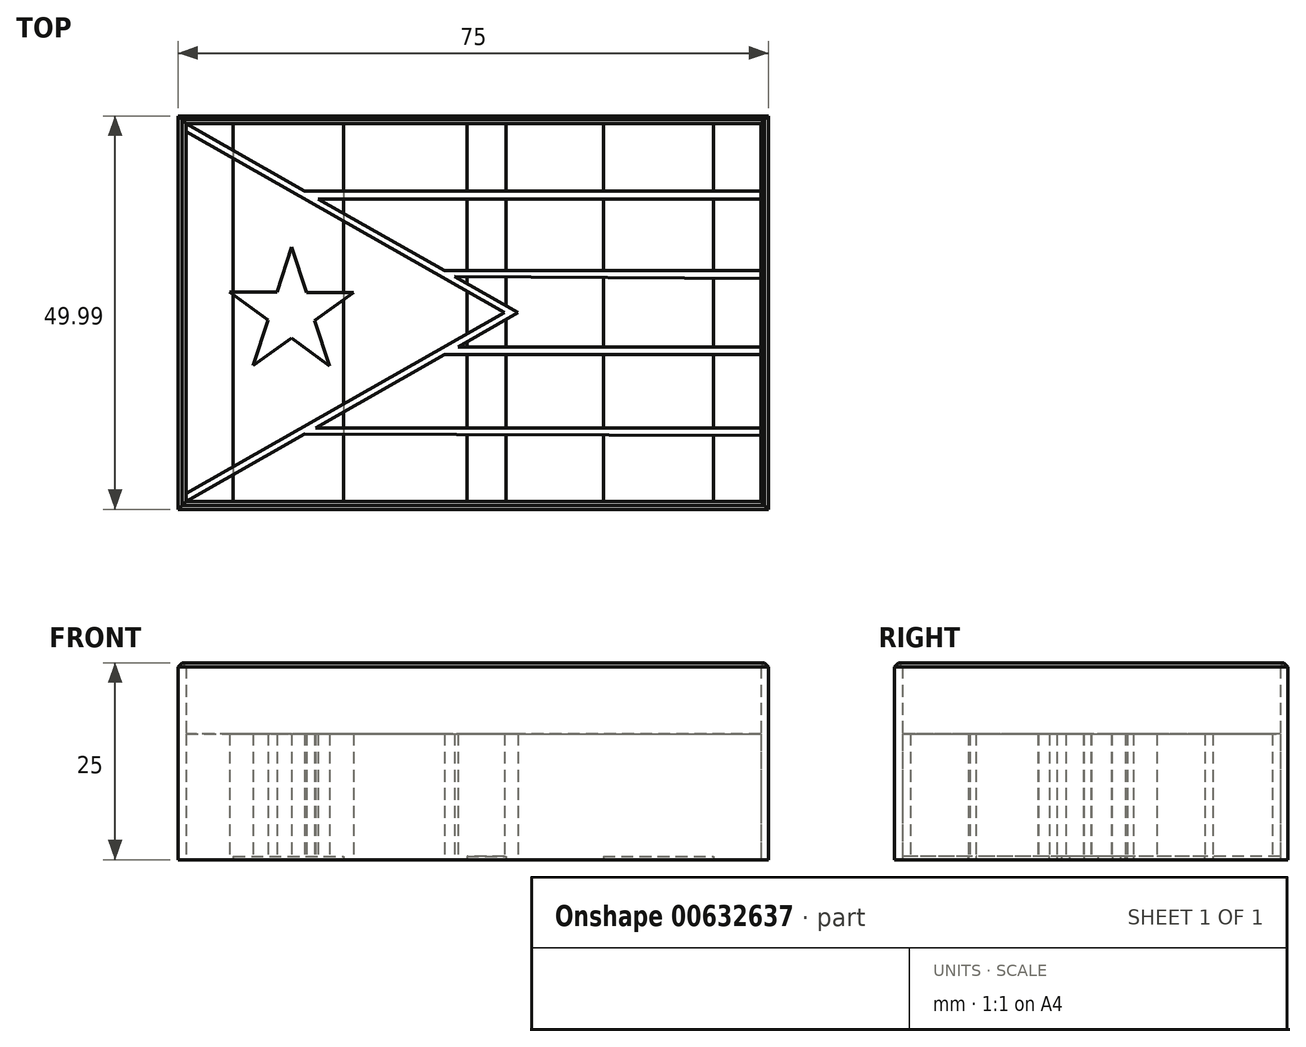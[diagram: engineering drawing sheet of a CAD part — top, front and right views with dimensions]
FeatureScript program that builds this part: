
annotation { "Feature Type Name" : "Feature", "Feature Type Description" : "" }
export const myFeature = defineFeature(function(context is Context, id is Id, definition is map)
    precondition{}
    {
        {
            var Q0;
            Q0=qCreatedBy(makeId("Top.planeOp"),FACE);
            var sketch = newSketch(context, id + "F0", { "sketchPlane" : qUnion([Q0])});
            skSolve(sketch);
        }
        {
            var Q0;
            Q0=qCreatedBy(makeId("Top.planeOp"),FACE);
            var sketch = newSketch(context, id + "F1", { "sketchPlane" : qUnion([Q0])});
            skLineSegment(sketch, "E0.bottom", {"start": v(-39.18, 20.1) * mm, "end": v(35.82, 20.1) * mm});
            skLineSegment(sketch, "E0.top", {"start": v(-39.18, -29.88) * mm, "end": v(35.82, -29.88) * mm});
            skLineSegment(sketch, "E0.left", {"start": v(-39.18, 20.1) * mm, "end": v(-39.18, -29.88) * mm});
            skLineSegment(sketch, "E0.right", {"start": v(35.82, 20.1) * mm, "end": v(35.82, -29.88) * mm});
            skSolve(sketch);
        }
        {
            var Q0;
            Q0=makeQuery(id+"F1.imprint","IMPRINT",FACE,{"disambiguationData":[TD([[makeQuery(id+"F1.imprint","IMPRINT",EDGE,{"derivedFrom":sQuery(id+"F1.wireOp",EDGE,"E0.bottom")}),-1.0]])]});
            extrude(context, id + "F2", {"entities" : qUnion([Q0]), "depth" : 25 * mm, "offsetDistance" : 25 * mm});
        }
        {
            var Q0;
            Q0=qCreatedBy(makeId("Top.planeOp"),FACE);
            var sketch = newSketch(context, id + "F3", { "sketchPlane" : qUnion([Q0])});
            skLineSegment(sketch, "E1.bottom", {"start": v(-38.18, 19.1) * mm, "end": v(34.82, 19.1) * mm});
            skLineSegment(sketch, "E1.top", {"start": v(-38.18, -28.88) * mm, "end": v(34.82, -28.88) * mm});
            skLineSegment(sketch, "E1.left", {"start": v(-38.18, 19.1) * mm, "end": v(-38.18, -28.88) * mm});
            skLineSegment(sketch, "E1.right", {"start": v(34.82, 19.1) * mm, "end": v(34.82, -28.88) * mm});
            skLineSegment(sketch, "E2", {"start": v(34.82, 19.1) * mm, "end": v(35.82, 19.1) * mm});
            skLineSegment(sketch, "E3", {"start": v(34.82, 19.1) * mm, "end": v(34.82, 20.1) * mm});
            skLineSegment(sketch, "E4", {"start": v(-38.18, 19.1) * mm, "end": v(-39.18, 19.1) * mm});
            skLineSegment(sketch, "E5", {"start": v(-38.18, -28.88) * mm, "end": v(-38.18, -29.88) * mm});
            skSolve(sketch);
        }
        {
            var Q0;
            Q0 = qSketchRegion(id + "F3", true);
            extrude(context, id + "F4", {"entities" : qUnion([Q0]), "operationType" : NewBodyOperationType.REMOVE, "depth" : 25 * mm, "offsetDistance" : 25 * mm});
        }
        {
            var Q0;
            Q0=makeQuery(id+"F2.opExtrude","CAP_FACE",FACE,{"disambiguationData":[OSD([sQuery(id+"F1.wireOp",EDGE,"E0.bottom"),sQuery(id+"F1.wireOp",EDGE,"E0.top"),sQuery(id+"F1.wireOp",EDGE,"E0.left"),sQuery(id+"F1.wireOp",EDGE,"E0.right")])],"isStart":false});
            chamfer(context, id + "F5", {"entities" : qUnion([Q0]), "chamferType" : ChamferType.OFFSET_ANGLE, "width" : .5 * mm, "oppositeDirection" : false, "angle" : 45 * degree, "tangentPropagation" : true});
        }
        {
            var Q0;
            Q0=qCreatedBy(makeId("Top.planeOp"),FACE);
            var sketch = newSketch(context, id + "F6", { "sketchPlane" : qUnion([Q0])});
            skLineSegment(sketch, "E6", {"start": v(-38.18, 19.1) * mm, "end": v(4.02, -4.9) * mm});
            skLineSegment(sketch, "E7", {"start": v(4.02, -4.9) * mm, "end": v(-38.18, -28.88) * mm});
            skLineSegment(sketch, "E8", {"start": v(-38.18, -28.88) * mm, "end": v(-38.18, 19.1) * mm});
            skSolve(sketch);
        }
        {
            var Q0;
            Q0=makeQuery(id+"F6.imprint","IMPRINT",FACE,{"disambiguationData":[TD([[makeQuery(id+"F6.imprint","IMPRINT",EDGE,{"derivedFrom":sQuery(id+"F6.wireOp",EDGE,"E6")}),-1.0]])]});
            extrude(context, id + "F7", {"entities" : qUnion([Q0]), "operationType" : NewBodyOperationType.ADD, "depth" : 16 * mm, "offsetDistance" : 25 * mm});
        }
        {
            var Q0;
            Q0=qCreatedBy(makeId("Top.planeOp"),FACE);
            var sketch = newSketch(context, id + "F8", { "sketchPlane" : qUnion([Q0])});
            skLineSegment(sketch, "E9", {"start": v(-38.17, 18.1) * mm, "end": v(2.27, -4.9) * mm});
            skLineSegment(sketch, "E10", {"start": v(2.27, -4.9) * mm, "end": v(-38.17, -27.88) * mm});
            skLineSegment(sketch, "E11", {"start": v(-38.17, -27.88) * mm, "end": v(-38.17, 18.1) * mm});
            skLineSegment(sketch, "E12", {"start": v(-38.17, 19.1) * mm, "end": v(-38.17, 18.1) * mm});
            skLineSegment(sketch, "E13", {"start": v(-38.17, -28.88) * mm, "end": v(-38.17, -27.88) * mm});
            skSolve(sketch);
        }
        {
            var Q0;
            Q0 = qSketchRegion(id + "F8", true);
            extrude(context, id + "F9", {"entities" : qUnion([Q0]), "operationType" : NewBodyOperationType.REMOVE, "depth" : 16 * mm, "offsetDistance" : 25 * mm});
        }
        {
            var Q0;
            Q0=qCreatedBy(makeId("Top.planeOp"),FACE);
            var sketch = newSketch(context, id + "F10", { "sketchPlane" : qUnion([Q0])});
            skLineSegment(sketch, "E14", {"start": v(-23.14, 10.55) * mm, "end": v(34.82, 10.55) * mm});
            skLineSegment(sketch, "E15", {"start": v(34.82, 10.55) * mm, "end": v(34.82, 9.55) * mm});
            skLineSegment(sketch, "E16", {"start": v(34.82, 9.55) * mm, "end": v(-21.38, 9.55) * mm});
            skLineSegment(sketch, "E17", {"start": v(-21.38, 9.55) * mm, "end": v(-23.14, 10.55) * mm});
            skSolve(sketch);
        }
        {
            var Q0;
            Q0=makeQuery(id+"F10.imprint","IMPRINT",FACE,{"disambiguationData":[TD([[makeQuery(id+"F10.imprint","IMPRINT",EDGE,{"derivedFrom":sQuery(id+"F10.wireOp",EDGE,"E14")}),-1.0]])]});
            extrude(context, id + "F11", {"entities" : qUnion([Q0]), "operationType" : NewBodyOperationType.ADD, "depth" : 16 * mm, "offsetDistance" : 25 * mm});
        }
        {
            var Q0;
            Q0=qCreatedBy(makeId("Top.planeOp"),FACE);
            var sketch = newSketch(context, id + "F12", { "sketchPlane" : qUnion([Q0])});
            skLineSegment(sketch, "E18", {"start": v(-5.36, 0.44) * mm, "end": v(34.82, 0.44) * mm});
            skLineSegment(sketch, "E19", {"start": v(34.82, 0.44) * mm, "end": v(34.82, -0.56) * mm});
            skLineSegment(sketch, "E20", {"start": v(34.82, -0.56) * mm, "end": v(-4.04, -0.31) * mm});
            skLineSegment(sketch, "E21", {"start": v(-4.04, -0.31) * mm, "end": v(-5.36, 0.44) * mm});
            skSolve(sketch);
        }
        {
            var Q0;
            Q0 = qSketchRegion(id + "F12", true);
            extrude(context, id + "F13", {"entities" : qUnion([Q0]), "operationType" : NewBodyOperationType.ADD, "depth" : 16 * mm, "offsetDistance" : 25 * mm});
        }
        {
            var Q0;
            Q0=qCreatedBy(makeId("Top.planeOp"),FACE);
            var sketch = newSketch(context, id + "F14", { "sketchPlane" : qUnion([Q0])});
            skLineSegment(sketch, "E22", {"start": v(-3.6, -9.23) * mm, "end": v(34.82, -9.23) * mm});
            skLineSegment(sketch, "E23", {"start": v(34.82, -9.23) * mm, "end": v(34.82, -10.23) * mm});
            skLineSegment(sketch, "E24", {"start": v(34.82, -10.23) * mm, "end": v(-5.36, -10.23) * mm});
            skLineSegment(sketch, "E25", {"start": v(-5.36, -10.23) * mm, "end": v(-3.6, -9.23) * mm});
            skSolve(sketch);
        }
        {
            var Q0;
            Q0 = qSketchRegion(id + "F14", true);
            extrude(context, id + "F15", {"entities" : qUnion([Q0]), "operationType" : NewBodyOperationType.ADD, "depth" : 16 * mm, "offsetDistance" : 25 * mm});
        }
        {
            var Q0;
            Q0=qCreatedBy(makeId("Top.planeOp"),FACE);
            var sketch = newSketch(context, id + "F16", { "sketchPlane" : qUnion([Q0])});
            skLineSegment(sketch, "E26", {"start": v(-23.14, -20.33) * mm, "end": v(-21.7, -19.51) * mm});
            skLineSegment(sketch, "E27", {"start": v(-21.7, -19.51) * mm, "end": v(34.82, -19.51) * mm});
            skLineSegment(sketch, "E28", {"start": v(34.82, -19.51) * mm, "end": v(34.82, -20.51) * mm});
            skLineSegment(sketch, "E29", {"start": v(34.82, -20.51) * mm, "end": v(-23.14, -20.33) * mm});
            skSolve(sketch);
        }
        {
            var Q0;
            Q0=makeQuery(id+"F16.imprint","IMPRINT",FACE,{"disambiguationData":[TD([[makeQuery(id+"F16.imprint","IMPRINT",EDGE,{"derivedFrom":sQuery(id+"F16.wireOp",EDGE,"E26")}),-1.0]])]});
            extrude(context, id + "F17", {"entities" : qUnion([Q0]), "operationType" : NewBodyOperationType.ADD, "depth" : 16 * mm, "offsetDistance" : 25 * mm});
        }
        {
            var Q0;
            Q0=qCreatedBy(makeId("Top.planeOp"),FACE);
            var sketch = newSketch(context, id + "F18", { "sketchPlane" : qUnion([Q0])});
            skLineSegment(sketch, "E30", {"start": v(-24.78, 3.43) * mm, "end": v(-26.63, -2.28) * mm});
            skLineSegment(sketch, "E31", {"start": v(-26.63, -2.28) * mm, "end": v(-32.61, -2.28) * mm});
            skLineSegment(sketch, "E32", {"start": v(-32.61, -2.28) * mm, "end": v(-27.77, -5.84) * mm});
            skLineSegment(sketch, "E33", {"start": v(-27.77, -5.84) * mm, "end": v(-29.65, -11.63) * mm});
            skLineSegment(sketch, "E34", {"start": v(-29.65, -11.63) * mm, "end": v(-24.77, -8.1) * mm});
            skLineSegment(sketch, "E35", {"start": v(-24.77, -8.1) * mm, "end": v(-19.93, -11.65) * mm});
            skLineSegment(sketch, "E36", {"start": v(-19.93, -11.65) * mm, "end": v(-21.86, -5.9) * mm});
            skLineSegment(sketch, "E37", {"start": v(-21.86, -5.9) * mm, "end": v(-16.88, -2.3) * mm});
            skLineSegment(sketch, "E38", {"start": v(-16.88, -2.3) * mm, "end": v(-22.86, -2.3) * mm});
            skLineSegment(sketch, "E39", {"start": v(-22.86, -2.3) * mm, "end": v(-24.78, 3.43) * mm});
            skSolve(sketch);
        }
        {
            var Q0;
            Q0=makeQuery(id+"F18.imprint","IMPRINT",FACE,{"disambiguationData":[TD([[makeQuery(id+"F18.imprint","IMPRINT",EDGE,{"derivedFrom":sQuery(id+"F18.wireOp",EDGE,"E30")}),1.0]])]});
            extrude(context, id + "F19", {"entities" : qUnion([Q0]), "depth" : 16 * mm, "offsetDistance" : 25 * mm});
        }
        {
            var Q0;
            Q0=qCreatedBy(makeId("Top.planeOp"),FACE);
            var sketch = newSketch(context, id + "F20", { "sketchPlane" : qUnion([Q0])});
            skLineSegment(sketch, "E40.bottom", {"start": v(-32.18, 19.1) * mm, "end": v(-18.18, 19.1) * mm});
            skLineSegment(sketch, "E40.top", {"start": v(-32.18, -28.88) * mm, "end": v(-18.18, -28.88) * mm});
            skLineSegment(sketch, "E40.left", {"start": v(-32.18, 19.1) * mm, "end": v(-32.18, -28.88) * mm});
            skLineSegment(sketch, "E40.right", {"start": v(-18.18, 19.1) * mm, "end": v(-18.18, -28.88) * mm});
            skLineSegment(sketch, "E41", {"start": v(-32.18, 8.04) * mm, "end": v(-38.18, 8.04) * mm});
            skSolve(sketch);
        }
        {
            var Q0;
            Q0 = qSketchRegion(id + "F20", true);
            extrude(context, id + "F21", {"entities" : qUnion([Q0]), "depth" : .4 * mm, "offsetDistance" : 25 * mm});
        }
        {
            var Q0;
            Q0=qCreatedBy(makeId("Top.planeOp"),FACE);
            var sketch = newSketch(context, id + "F22", { "sketchPlane" : qUnion([Q0])});
            skLineSegment(sketch, "E42.bottom", {"start": v(14.82, 19.1) * mm, "end": v(28.82, 19.1) * mm});
            skLineSegment(sketch, "E42.top", {"start": v(14.82, -29.88) * mm, "end": v(28.82, -29.88) * mm});
            skLineSegment(sketch, "E42.left", {"start": v(14.82, 19.1) * mm, "end": v(14.82, -29.88) * mm});
            skLineSegment(sketch, "E42.right", {"start": v(28.82, 19.1) * mm, "end": v(28.82, -29.88) * mm});
            skLineSegment(sketch, "E43", {"start": v(28.82, 4.27) * mm, "end": v(34.82, 4.27) * mm});
            skSolve(sketch);
        }
        {
            var Q0;
            Q0 = qSketchRegion(id + "F22", true);
            extrude(context, id + "F23", {"entities" : qUnion([Q0]), "operationType" : NewBodyOperationType.ADD, "depth" : .4 * mm, "offsetDistance" : 25 * mm});
        }
        {
            var Q0;
            Q0=qCreatedBy(makeId("Top.planeOp"),FACE);
            var sketch = newSketch(context, id + "F24", { "sketchPlane" : qUnion([Q0])});
            skLineSegment(sketch, "E44.bottom", {"start": v(-2.5, 19.1) * mm, "end": v(2.5, 19.1) * mm});
            skLineSegment(sketch, "E44.top", {"start": v(-2.5, -28.88) * mm, "end": v(2.5, -28.88) * mm});
            skLineSegment(sketch, "E44.left", {"start": v(-2.5, 19.1) * mm, "end": v(-2.5, -28.88) * mm});
            skLineSegment(sketch, "E44.right", {"start": v(2.5, 19.1) * mm, "end": v(2.5, -28.88) * mm});
            skLineSegment(sketch, "E45", {"start": v(0, 7.04) * mm, "end": v(2.5, 7.04) * mm});
            skSolve(sketch);
        }
        {
            var Q0;
            Q0=makeQuery(id+"F24.imprint","IMPRINT",FACE,{"disambiguationData":[TD([[makeQuery(id+"F24.imprint","IMPRINT",EDGE,{"derivedFrom":sQuery(id+"F24.wireOp",EDGE,"E44.bottom")}),-1.0]])]});
            extrude(context, id + "F25", {"entities" : qUnion([Q0]), "operationType" : NewBodyOperationType.ADD, "depth" : .4 * mm, "offsetDistance" : 25 * mm});
        }
    });
